# Revit family: Door_Protection-Construction_Specialties-Kick_Plate-KP-40N-60N
name_source: partatom
category: Specialty Equipment
revit_build: Autodesk Revit 2017 (Build: 20160225_1515(x64)
units: mm (PartAtom-declared; Revit-internal decimal feet)

## family parameters
Cut with Voids When Loaded = No
Host = Face
OmniClass Number = 23.30.10.11.34
OmniClass Title = Door Accessories
Part Type = Normal
Room Calculation Point = No
Round Connector Dimension = Use Diameter
Shared = No

## types (2) — shared parameters
Assembly Code = C1020410
Default Elevation = 4' - 0"
Description = Acrovyn Kick Plate
Manufacturer = Construction Specialties
Product Documentation Link = https://www.c-sgroup.com
Product Page URL = https://www.c-sgroup.com
URL = https://www.c-sgroup.com

## per-type parameters (varying)
| type | 40N | 60N | Thickness |
| KP-40N | Yes | No | 0' - 0 1/32" |
| KP-60N | No | Yes | 0' - 0 1/16" |

note: column(s) folded — value = type name in every type: Model

## geometry (parser evidence)
native form markers: Sweep x3
no freeform markers — native parametric forms only
